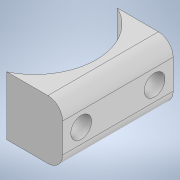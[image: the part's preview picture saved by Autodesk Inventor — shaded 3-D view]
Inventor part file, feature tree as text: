
AUTODESK INVENTOR PART (.ipt)
format: ipt  version: 2020 (Build 240168000, 168)  size: 141,312 bytes
history: native  units: in
note: dims shown in document units (in); Inventor stores cm internally (conversion verified against a paired STEP export)
features: sketch x3, extrude x2, hole x1, fillet x1
ambient origin geometry x8: Origin, YZ Plane, XZ Plane, XY Plane, X Axis, Y Axis, Z Axis, Center Point
bodies: Solid1 (feature_tree)
feature tree (7):
  extrude  "Extrusion1"  Depth=1.04in
  hole  "Hole1"  [1 undecoded]
  fillet  "Fillet1"  Radius=1.05in
  extrude  "Extrusion2"  Depth=0.125in
  sketch  "Sketch1"  dims[d0=1.04in d1=1.04in]
  sketch  "Sketch2"  dims[d2=0.708in d3=0.0in d4=1.05in]
  sketch  "Sketch3"  dims[d5=0.5in d6=0.0in d7=0.25in d8=90.0deg d9=0.312in d10=0.0in d11=0.312in d12=180.0deg d13=0.177in d14=0.75in d15=0.332in d16=0.25in d17=0.5635in d18=1.378in d19=0.0in d20=0.125in d21=0.05in d22=0.05in d23=1.0in d24=0.0in]
note: 1 required parameter value undecoded (feature->parameter linkage not recoverable at this tier; creation-order binding heuristic only, values carry confidence <= 0.55)
